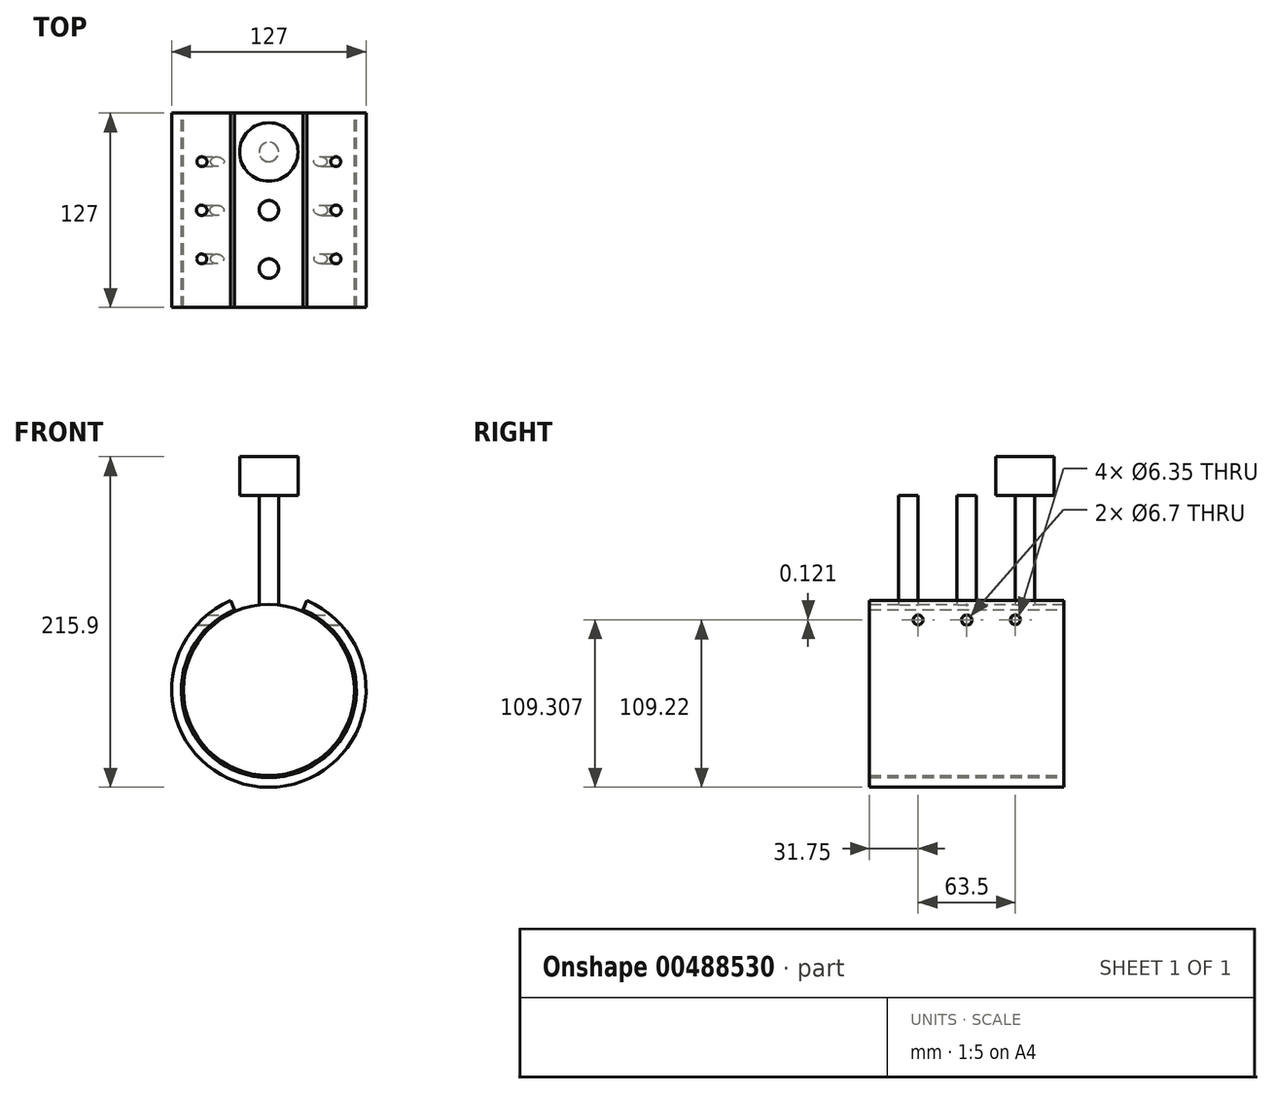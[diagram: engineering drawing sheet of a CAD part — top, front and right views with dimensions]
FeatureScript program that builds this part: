
annotation { "Feature Type Name" : "Feature", "Feature Type Description" : "" }
export const myFeature = defineFeature(function(context is Context, id is Id, definition is map)
    precondition{}
    {
        {
            var Q0;
            Q0=qCreatedBy(makeId("Front.planeOp"),FACE);
            var sketch = newSketch(context, id + "F0", { "sketchPlane" : qUnion([Q0])});
            skArc(sketch, "E0", {"start": v(-24.89, 58.42) * mm, "mid": v(0, -63.5) * mm, "end": v(24.89, 58.42) * mm});
            skArc(sketch, "E1", {"start": v(-22.4, 52.58) * mm, "mid": v(0, -57.15) * mm, "end": v(22.4, 52.58) * mm});
            skLineSegment(sketch, "E2", {"start": v(-22.4, 52.58) * mm, "end": v(-24.89, 58.42) * mm});
            skLineSegment(sketch, "E3", {"start": v(22.4, 52.58) * mm, "end": v(24.89, 58.42) * mm});
            skPoint(sketch, "E4.orphan", {"position": v(0, 63.5) * mm});
            skSolve(sketch);
        }
        {
            var Q0;
            Q0 = qSketchRegion(id + "F0", true);
            extrude(context, id + "F1", {"entities" : qUnion([Q0]), "endBound" : BoundingType.SYMMETRIC, "depth" : 127 * mm});
        }
        {
            var Q0;
            Q0=qCreatedBy(makeId("Right.planeOp"),FACE);
            var sketch = newSketch(context, id + "F2", { "sketchPlane" : qUnion([Q0])});
            skLineSegment(sketch, "E5.0", {"start": v(-63.5, 58.42) * mm, "end": v(63.5, 58.42) * mm});
            skLineSegment(sketch, "E6", {"start": v(0, 58.42) * mm, "end": v(0, 45.72) * mm, "construction": true});
            skLineSegment(sketch, "E7", {"start": v(0, 45.72) * mm, "end": v(61.86, 45.72) * mm, "construction": true});
            skLineSegment(sketch, "E8", {"start": v(0, 45.72) * mm, "end": v(-68.06, 45.72) * mm, "construction": true});
            skCircle(sketch, "E9", {"center": v(0, 45.72) * mm, "radius": 3.35 * mm});
            skCircle(sketch, "E10", {"center": v(-31.75, 45.8) * mm, "radius": 3.18 * mm});
            skCircle(sketch, "E11", {"center": v(31.75, 45.93) * mm, "radius": 3.18 * mm});
            skSolve(sketch);
        }
        {
            var Q0;
            Q0 = qSketchRegion(id + "F2", true);
            extrude(context, id + "F3", {"entities" : qUnion([Q0]), "operationType" : NewBodyOperationType.REMOVE, "endBound" : BoundingType.SYMMETRIC, "oppositeDirection" : true, "depth" : 152.4 * mm});
        }
        {
            var Q0;
            Q0=qCreatedBy(makeId("Front.planeOp"),FACE);
            var sketch = newSketch(context, id + "F4", { "sketchPlane" : qUnion([Q0])});
            skCircle(sketch, "E12", {"center": v(0, 0) * mm, "radius": 55.88 * mm});
            skSolve(sketch);
        }
        {
            var Q0;
            Q0 = qSketchRegion(id + "F4", true);
            extrude(context, id + "F5", {"entities" : qUnion([Q0]), "endBound" : BoundingType.SYMMETRIC, "depth" : 127 * mm});
        }
        {
            var Q0;
            Q0=qCreatedBy(makeId("Top.planeOp"),FACE);
            var sketch = newSketch(context, id + "F6", { "sketchPlane" : qUnion([Q0])});
            skCircle(sketch, "E13", {"center": v(0, 0) * mm, "radius": 6.35 * mm});
            skCircle(sketch, "E14", {"center": v(0, -38.1) * mm, "radius": 6.35 * mm});
            skCircle(sketch, "E15", {"center": v(0, 38.1) * mm, "radius": 6.35 * mm});
            skSolve(sketch);
        }
        {
            var Q0;
            Q0 = qSketchRegion(id + "F6", true);
            extrude(context, id + "F7", {"entities" : qUnion([Q0]), "operationType" : NewBodyOperationType.ADD, "depth" : 127 * mm});
        }
        {
            var Q0;
            Q0=makeQuery(id+"F7.opExtrude","CAP_FACE",FACE,{"disambiguationData":[OSD([sQuery(id+"F6.wireOp",EDGE,"E15")])],"isStart":false});
            var sketch = newSketch(context, id + "F8", { "sketchPlane" : qUnion([Q0])});
            skCircle(sketch, "E16", {"center": v(0, 38.1) * mm, "radius": 19.05 * mm});
            skSolve(sketch);
        }
        {
            var Q0;
            Q0 = qSketchRegion(id + "F8", true);
            extrude(context, id + "F9", {"entities" : qUnion([Q0]), "operationType" : NewBodyOperationType.ADD, "depth" : 25.4 * mm});
        }
    });
